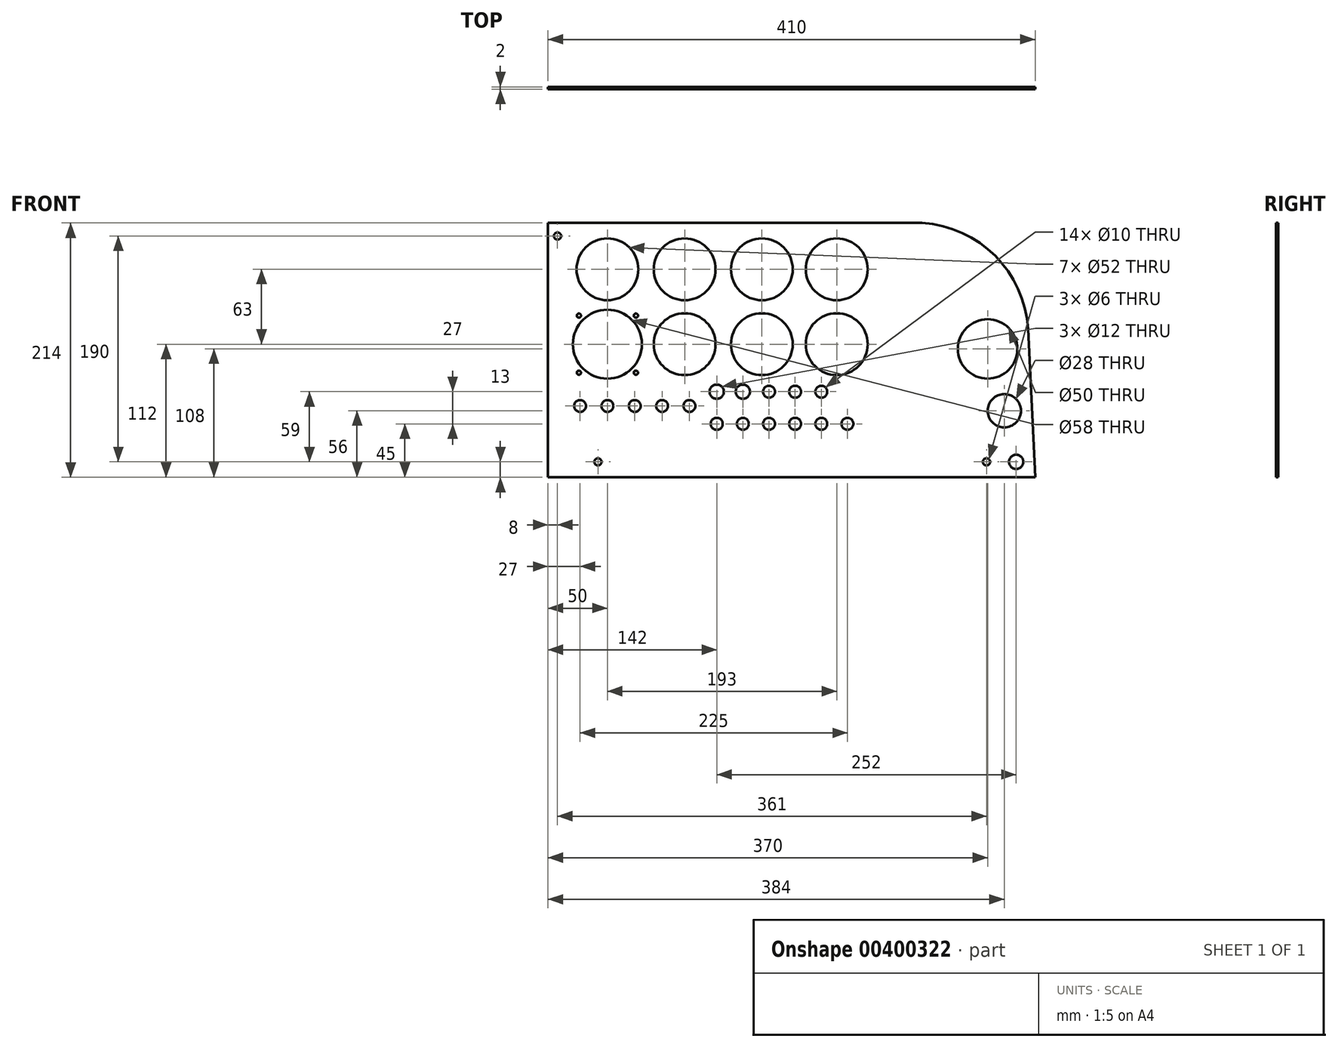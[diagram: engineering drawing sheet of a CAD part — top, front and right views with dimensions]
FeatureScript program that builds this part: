
annotation { "Feature Type Name" : "Feature", "Feature Type Description" : "" }
export const myFeature = defineFeature(function(context is Context, id is Id, definition is map)
    precondition{}
    {
        {
            var Q0;
            Q0=qCreatedBy(makeId("Front.planeOp"),FACE);
            var sketch = newSketch(context, id + "F0", { "sketchPlane" : qUnion([Q0])});
            skLineSegment(sketch, "E0", {"start": v(0, 0) * mm, "end": v(410, 0) * mm});
            skLineSegment(sketch, "E1", {"start": v(0, 0) * mm, "end": v(0, 214) * mm});
            skLineSegment(sketch, "E2", {"start": v(0, 214) * mm, "end": v(315, 214) * mm});
            skLineSegment(sketch, "E3", {"start": v(410, 0) * mm, "end": v(404, 125) * mm});
            skArc(sketch, "E4", {"start": v(404, 125) * mm, "mid": v(374.15, 188.4) * mm, "end": v(309, 214.19) * mm});
            skLineSegment(sketch, "E5", {"start": v(-61.3, 112) * mm, "end": v(397.46, 112) * mm, "construction": true});
            skLineSegment(sketch, "E6", {"start": v(-104.48, 175) * mm, "end": v(334.48, 175) * mm, "construction": true});
            skCircle(sketch, "E7", {"center": v(50, 175) * mm, "radius": 26 * mm});
            skCircle(sketch, "E8", {"center": v(115, 175) * mm, "radius": 26 * mm});
            skCircle(sketch, "E9", {"center": v(180, 175) * mm, "radius": 26 * mm});
            skCircle(sketch, "E10", {"center": v(243, 175) * mm, "radius": 26 * mm});
            skLineSegment(sketch, "E11", {"start": v(50, 175) * mm, "end": v(50, 100.02) * mm, "construction": true});
            skLineSegment(sketch, "E12", {"start": v(115, 175) * mm, "end": v(115, 102.57) * mm, "construction": true});
            skLineSegment(sketch, "E13", {"start": v(180, 175) * mm, "end": v(180, 100.56) * mm, "construction": true});
            skLineSegment(sketch, "E14", {"start": v(243, 175) * mm, "end": v(243, 105.08) * mm, "construction": true});
            skCircle(sketch, "E15", {"center": v(50, 112) * mm, "radius": 29 * mm});
            skCircle(sketch, "E16", {"center": v(115, 112) * mm, "radius": 26 * mm});
            skCircle(sketch, "E17", {"center": v(180, 112) * mm, "radius": 26 * mm});
            skCircle(sketch, "E18", {"center": v(243, 112) * mm, "radius": 26 * mm});
            skLineSegment(sketch, "E19", {"start": v(135.88, 72) * mm, "end": v(216.86, 72) * mm, "construction": true});
            skLineSegment(sketch, "E20", {"start": v(135.9, 45) * mm, "end": v(252.98, 45) * mm, "construction": true});
            skCircle(sketch, "E21", {"center": v(142, 72) * mm, "radius": 6 * mm});
            skCircle(sketch, "E22.1.0.0", {"center": v(164, 72) * mm, "radius": 6 * mm});
            skLineSegment(sketch, "E22.direction1", {"start": v(142, 72) * mm, "end": v(164, 72) * mm, "construction": true});
            skCircle(sketch, "E23", {"center": v(142, 45) * mm, "radius": 5 * mm});
            skCircle(sketch, "E24.1.0.0", {"center": v(164, 45) * mm, "radius": 5 * mm});
            skCircle(sketch, "E24.2.0.0", {"center": v(186, 45) * mm, "radius": 5 * mm});
            skCircle(sketch, "E24.3.0.0", {"center": v(208, 45) * mm, "radius": 5 * mm});
            skCircle(sketch, "E24.4.0.0", {"center": v(230, 45) * mm, "radius": 5 * mm});
            skLineSegment(sketch, "E24.direction1", {"start": v(142, 45) * mm, "end": v(164, 45) * mm, "construction": true});
            skCircle(sketch, "E25", {"center": v(186, 72) * mm, "radius": 5 * mm});
            skCircle(sketch, "E26.1.0.0", {"center": v(208, 72) * mm, "radius": 5 * mm});
            skLineSegment(sketch, "E26.1.0.1", {"start": v(157.88, 72) * mm, "end": v(238.86, 72) * mm, "construction": true});
            skCircle(sketch, "E26.2.0.0", {"center": v(230, 72) * mm, "radius": 5 * mm});
            skLineSegment(sketch, "E26.2.0.1", {"start": v(179.88, 72) * mm, "end": v(260.86, 72) * mm, "construction": true});
            skLineSegment(sketch, "E26.direction1", {"start": v(186, 72) * mm, "end": v(208, 72) * mm, "construction": true});
            skCircle(sketch, "E27", {"center": v(50, 60) * mm, "radius": 5 * mm});
            skCircle(sketch, "E28.1.0.0", {"center": v(73, 60) * mm, "radius": 5 * mm});
            skCircle(sketch, "E28.2.0.0", {"center": v(96, 60) * mm, "radius": 5 * mm});
            skLineSegment(sketch, "E28.direction1", {"start": v(50, 60) * mm, "end": v(73, 60) * mm, "construction": true});
            skCircle(sketch, "E29.0.3.0", {"center": v(119, 60) * mm, "radius": 5 * mm});
            skLineSegment(sketch, "E30.direction1", {"start": v(50, 60) * mm, "end": v(27, 60) * mm, "construction": true});
            skCircle(sketch, "E31.0.1.0", {"center": v(27, 60) * mm, "radius": 5 * mm});
            skLineSegment(sketch, "E32", {"start": v(16.05, 88) * mm, "end": v(78.56, 88) * mm, "construction": true});
            skLineSegment(sketch, "E33", {"start": v(74, 142.36) * mm, "end": v(74, 85.1) * mm, "construction": true});
            skLineSegment(sketch, "E34", {"start": v(26, 85.5) * mm, "end": v(26, 143.55) * mm, "construction": true});
            skLineSegment(sketch, "E35", {"start": v(77.12, 136) * mm, "end": v(42, 136) * mm, "construction": true});
            skCircle(sketch, "E36", {"center": v(26, 136) * mm, "radius": 1.75 * mm});
            skCircle(sketch, "E37", {"center": v(26, 88) * mm, "radius": 1.75 * mm});
            skCircle(sketch, "E38", {"center": v(74, 88) * mm, "radius": 1.75 * mm});
            skCircle(sketch, "E39", {"center": v(74, 136) * mm, "radius": 1.75 * mm});
            skCircle(sketch, "E40", {"center": v(369, 13) * mm, "radius": 3 * mm});
            skLineSegment(sketch, "E41", {"start": v(363.52, 13) * mm, "end": v(396.35, 13) * mm, "construction": true});
            skCircle(sketch, "E42", {"center": v(394, 13) * mm, "radius": 6 * mm});
            skCircle(sketch, "E43", {"center": v(370, 108) * mm, "radius": 25 * mm});
            skCircle(sketch, "E44", {"center": v(384, 56) * mm, "radius": 14 * mm});
            skCircle(sketch, "E45.0.5.0", {"center": v(252, 45) * mm, "radius": 5 * mm});
            skCircle(sketch, "E46", {"center": v(8, 203) * mm, "radius": 3 * mm});
            skLineSegment(sketch, "E47", {"start": v(13.87, 13) * mm, "end": v(71.77, 13) * mm, "construction": true});
            skLineSegment(sketch, "E48", {"start": v(42, 20.01) * mm, "end": v(42, 4.42) * mm, "construction": true});
            skCircle(sketch, "E49", {"center": v(42, 13) * mm, "radius": 3 * mm});
            skSolve(sketch);
        }
        {
            var Q0;
            Q0=makeQuery(id+"F0.imprint","IMPRINT",FACE,{"disambiguationData":[TD([[makeQuery(id+"F0.imprint","IMPRINT",EDGE,{"derivedFrom":sQuery(id+"F0.wireOp",EDGE,"E0")}),1.0]])]});
            extrude(context, id + "F1", {"entities" : qUnion([Q0]), "depth" : 2 * mm, "offsetDistance" : 25 * mm});
        }
    });
